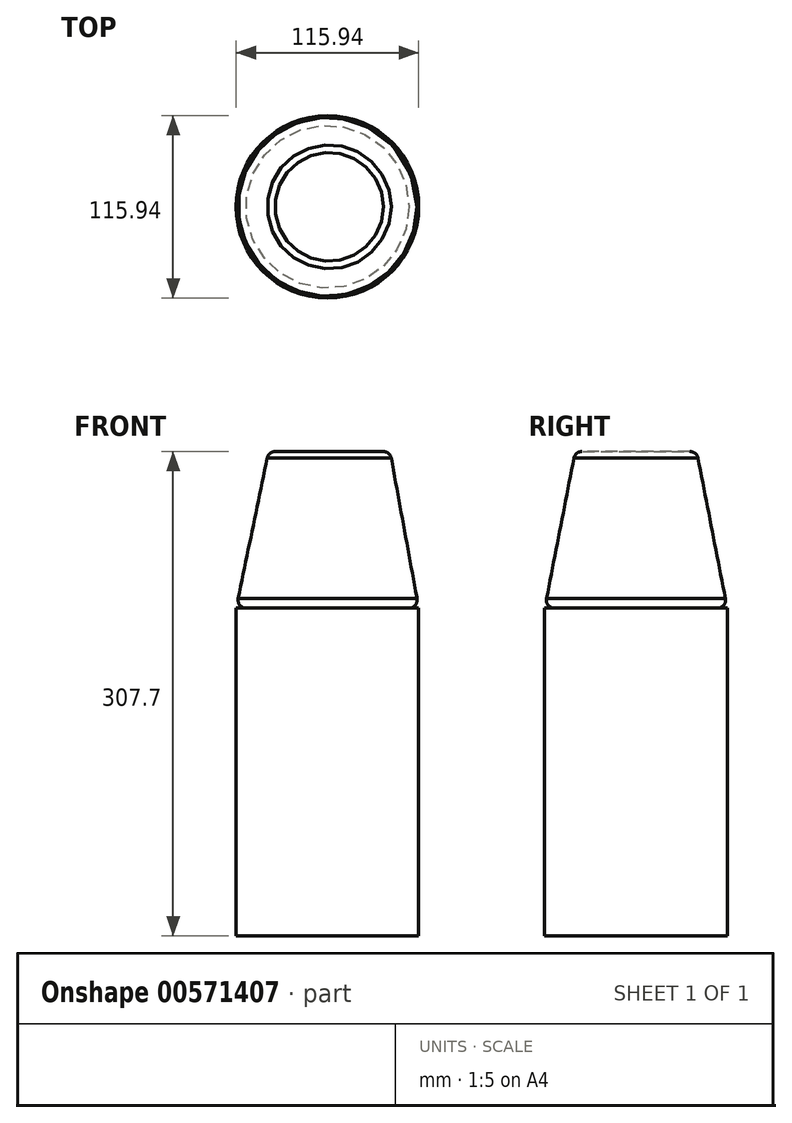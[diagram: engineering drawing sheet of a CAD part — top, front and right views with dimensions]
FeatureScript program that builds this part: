
annotation { "Feature Type Name" : "Feature", "Feature Type Description" : "" }
export const myFeature = defineFeature(function(context is Context, id is Id, definition is map)
    precondition{}
    {
        {
            var Q0;
            Q0=qCreatedBy(makeId("Top.planeOp"),FACE);
            var sketch = newSketch(context, id + "F0", { "sketchPlane" : qUnion([Q0])});
            skCircle(sketch, "E0", {"center": v(49.47, 0) * mm, "radius": 57.97 * mm});
            skSolve(sketch);
        }
        {
            var Q0;
            Q0=makeQuery(id+"F0.imprint","IMPRINT",FACE,{"disambiguationData":[TD([[makeQuery(id+"F0.imprint","IMPRINT",EDGE,{"derivedFrom":sQuery(id+"F0.wireOp",EDGE,"E0")}),1.0]])]});
            extrude(context, id + "F1", {"entities" : qUnion([Q0]), "depth" : 208.26 * mm, "offsetDistance" : 25.4 * mm});
        }
        {
            var Q0;
            Q0=makeQuery(id+"F1.opExtrude","CAP_FACE",FACE,{"disambiguationData":[OSD([sQuery(id+"F0.wireOp",EDGE,"E0")])],"isStart":false});
            var sketch = newSketch(context, id + "F2", { "sketchPlane" : qUnion([Q0])});
            skSolve(sketch);
        }
        {
            var Q0;
            Q0=makeQuery(id+"F2.imprint","IMPRINT",FACE,{"disambiguationData":[TD([[makeQuery(id+"F2.imprint","IMPRINT",EDGE,{"derivedFrom":makeQuery(id+"F1.opExtrude","CAP_EDGE",EDGE,{"disambiguationData":[OSD([sQuery(id+"F0.wireOp",EDGE,"E0")])],"isStart":false})}),1.0]])]});
            cPlane(context, id + "F3", {"entities" : qUnion([Q0]), "cplaneType" : CPlaneType.OFFSET, "offset" : 99.44 * mm, "width" : 152.4 * mm, "height" : 152.4 * mm});
        }
        {
            var Q0;
            Q0=qCreatedBy(id+"F3.planeOp",FACE);
            var sketch = newSketch(context, id + "F4", { "sketchPlane" : qUnion([Q0])});
            skCircle(sketch, "E1", {"center": v(50.63, 0) * mm, "radius": 38.6 * mm});
            skSolve(sketch);
        }
        {
            var Q0;
            Q0=makeQuery(id+"F2.imprint","IMPRINT",FACE,{"disambiguationData":[TD([[makeQuery(id+"F2.imprint","IMPRINT",EDGE,{"derivedFrom":makeQuery(id+"F1.opExtrude","CAP_EDGE",EDGE,{"disambiguationData":[OSD([sQuery(id+"F0.wireOp",EDGE,"E0")])],"isStart":false})}),1.0]])]});
            var Q1;
            Q1=makeQuery(id+"F4.imprint","IMPRINT",FACE,{"disambiguationData":[TD([[makeQuery(id+"F4.imprint","IMPRINT",EDGE,{"derivedFrom":sQuery(id+"F4.wireOp",EDGE,"E1")}),1.0]])]});
            loft(context, id + "F5", {"sheetProfilesArray" : [{ "sheetProfileEntities" : qUnion([Q0]) }, { "sheetProfileEntities" : qUnion([Q1]) }]});
        }
        {
            var Q0;
            Q0=makeQuery(id+"F5.opLoft","MID_CAP_EDGE",EDGE,{"disambiguationData":[OSD([sQuery(id+"F0.wireOp",EDGE,"E0")])],"capPos":0.0});
            fillet(context, id + "F6", {"entities" : qUnion([Q0]), "radius" : 5.08 * mm, "tangentPropagation" : true, "allowEdgeOverflow" : false});
        }
        {
            var Q0;
            Q0=makeQuery(id+"F5.opLoft","MID_CAP_EDGE",EDGE,{"disambiguationData":[OSD([sQuery(id+"F0.wireOp",EDGE,"E0"),sQuery(id+"F4.wireOp",EDGE,"E1")])],"capPos":1.0});
            fillet(context, id + "F7", {"entities" : qUnion([Q0]), "radius" : 5.08 * mm, "tangentPropagation" : true, "allowEdgeOverflow" : false});
        }
    });
